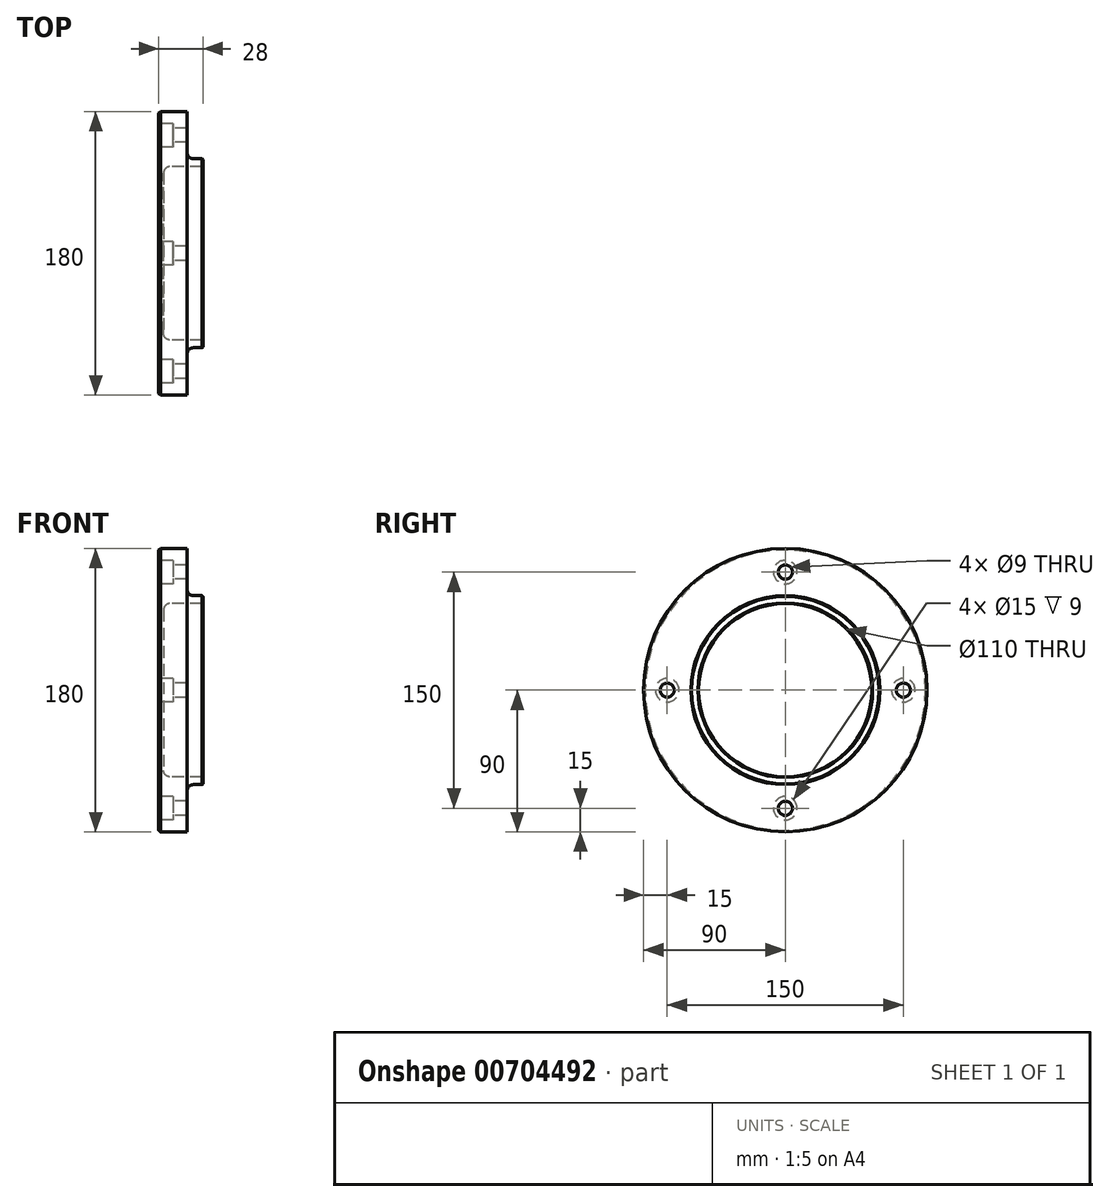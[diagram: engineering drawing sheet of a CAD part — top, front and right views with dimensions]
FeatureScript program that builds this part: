
annotation { "Feature Type Name" : "Feature", "Feature Type Description" : "" }
export const myFeature = defineFeature(function(context is Context, id is Id, definition is map)
    precondition{}
    {
        {
            var Q0;
            Q0=qCreatedBy(makeId("Front.planeOp"),FACE);
            var sketch = newSketch(context, id + "F0", { "sketchPlane" : qUnion([Q0])});
            skLineSegment(sketch, "E0", {"start": v(0, 90) * mm, "end": v(0, 0) * mm});
            skLineSegment(sketch, "E1", {"start": v(0, 0) * mm, "end": v(3, 0) * mm});
            skLineSegment(sketch, "E2", {"start": v(3, 0) * mm, "end": v(3, 55) * mm});
            skLineSegment(sketch, "E3", {"start": v(3, 55) * mm, "end": v(28, 55) * mm});
            skLineSegment(sketch, "E4", {"start": v(28, 55) * mm, "end": v(28, 60) * mm});
            skLineSegment(sketch, "E5", {"start": v(28, 60) * mm, "end": v(18, 60) * mm});
            skLineSegment(sketch, "E6", {"start": v(18, 60) * mm, "end": v(18, 90) * mm});
            skLineSegment(sketch, "E7", {"start": v(18, 90) * mm, "end": v(0, 90) * mm});
            skSolve(sketch);
        }
        {
            var Q0;
            Q0=makeQuery(id+"F0.imprint","IMPRINT",FACE,{"disambiguationData":[TD([[makeQuery(id+"F0.imprint","IMPRINT",EDGE,{"derivedFrom":sQuery(id+"F0.wireOp",EDGE,"E0")}),1.0]])]});
            var Q1;
            Q1=sQuery(id+"F0.wireOp",EDGE,"E1");
            revolve(context, id + "F1", {"surfaceOperationType" : NewSurfaceOperationType.NEW, "entities" : qUnion([Q0]), "axis" : qUnion([Q1]), "revolveType" : RevolveType.FULL});
        }
        {
            var Q0;
            Q0=makeQuery(id+"F1.opRevolve","SWEPT_FACE",FACE,{"disambiguationData":[OSD([sQuery(id+"F0.wireOp",EDGE,"E0")])]});
            var sketch = newSketch(context, id + "F2", { "sketchPlane" : qUnion([Q0])});
            skPoint(sketch, "E8", {"position": v(0, 75) * mm});
            skPoint(sketch, "E9", {"position": v(-75, 0) * mm});
            skPoint(sketch, "E10", {"position": v(75, 0) * mm});
            skPoint(sketch, "E11", {"position": v(0, -75) * mm});
            skCircle(sketch, "E12", {"center": v(0, 0) * mm, "radius": 75 * mm});
            skSolve(sketch);
        }
        {
            var Q0;
            Q0=sQuery(id+"F2.wireOp",VERTEX,"E8");
            var Q1;
            Q1=sQuery(id+"F2.wireOp",VERTEX,"E10");
            var Q2;
            Q2=sQuery(id+"F2.wireOp",VERTEX,"E11");
            var Q3;
            Q3=sQuery(id+"F2.wireOp",VERTEX,"E9");
            var Q4;
            Q4=makeQuery(id+"F1.opRevolve","SWEPT_BODY",BODY,{"disambiguationData":[OSD([sQuery(id+"F0.wireOp",EDGE,"E0"),sQuery(id+"F0.wireOp",EDGE,"E1"),sQuery(id+"F0.wireOp",EDGE,"E2"),sQuery(id+"F0.wireOp",EDGE,"E3"),sQuery(id+"F0.wireOp",EDGE,"E4"),sQuery(id+"F0.wireOp",EDGE,"E5"),sQuery(id+"F0.wireOp",EDGE,"E6"),sQuery(id+"F0.wireOp",EDGE,"E7")])]});
            hole(context, id + "F3", {"style" : HoleStyle.C_BORE, "endStyle" : HoleEndStyle.BLIND, "holeDiameter" : 9 * mm, "cBoreDiameter" : 15 * mm, "cBoreDepth" : 9 * mm, "majorDiameter" : 5 * mm, "holeDepth" : 18 * mm, "isTappedThrough" : true, "tappedDepth" : 12 * mm, "tapClearance" : 3, "locations" : qUnion([Q0, Q1, Q2, Q3]), "scope" : qUnion([Q4])});
        }
        {
            var Q0;
            Q0=makeQuery(id+"F1.opRevolve","SWEPT_EDGE",EDGE,{"disambiguationData":[OSD([sQuery(id+"F0.wireOp",EDGE,"E5"),sQuery(id+"F0.wireOp",EDGE,"E6")])]});
            fillet(context, id + "F4", {"entities" : qUnion([Q0]), "radius" : 4 * mm, "tangentPropagation" : true, "allowEdgeOverflow" : false});
        }
        {
            var Q0;
            Q0=makeQuery(id+"F1.opRevolve","SWEPT_EDGE",EDGE,{"disambiguationData":[OSD([sQuery(id+"F0.wireOp",EDGE,"E4"),sQuery(id+"F0.wireOp",EDGE,"E5")])]});
            var Q1;
            Q1=makeQuery(id+"F1.opRevolve","SWEPT_EDGE",EDGE,{"disambiguationData":[OSD([sQuery(id+"F0.wireOp",EDGE,"E3"),sQuery(id+"F0.wireOp",EDGE,"E4")])]});
            chamfer(context, id + "F5", {"entities" : qUnion([Q0, Q1]), "width" : 0.5 * mm, "tangentPropagation" : true});
        }
        {
            var Q0;
            Q0=makeQuery(id+"F1.opRevolve","SWEPT_EDGE",EDGE,{"disambiguationData":[OSD([sQuery(id+"F0.wireOp",EDGE,"E2"),sQuery(id+"F0.wireOp",EDGE,"E3")])]});
            fillet(context, id + "F6", {"entities" : qUnion([Q0]), "radius" : 4 * mm, "tangentPropagation" : true, "allowEdgeOverflow" : false});
        }
        {
            var Q0;
            Q0=makeQuery(id+"F1.opRevolve","SWEPT_EDGE",EDGE,{"disambiguationData":[OSD([sQuery(id+"F0.wireOp",EDGE,"E0"),sQuery(id+"F0.wireOp",EDGE,"E7")])]});
            chamfer(context, id + "F7", {"entities" : qUnion([Q0]), "width" : 1 * mm, "tangentPropagation" : true});
        }
    });
